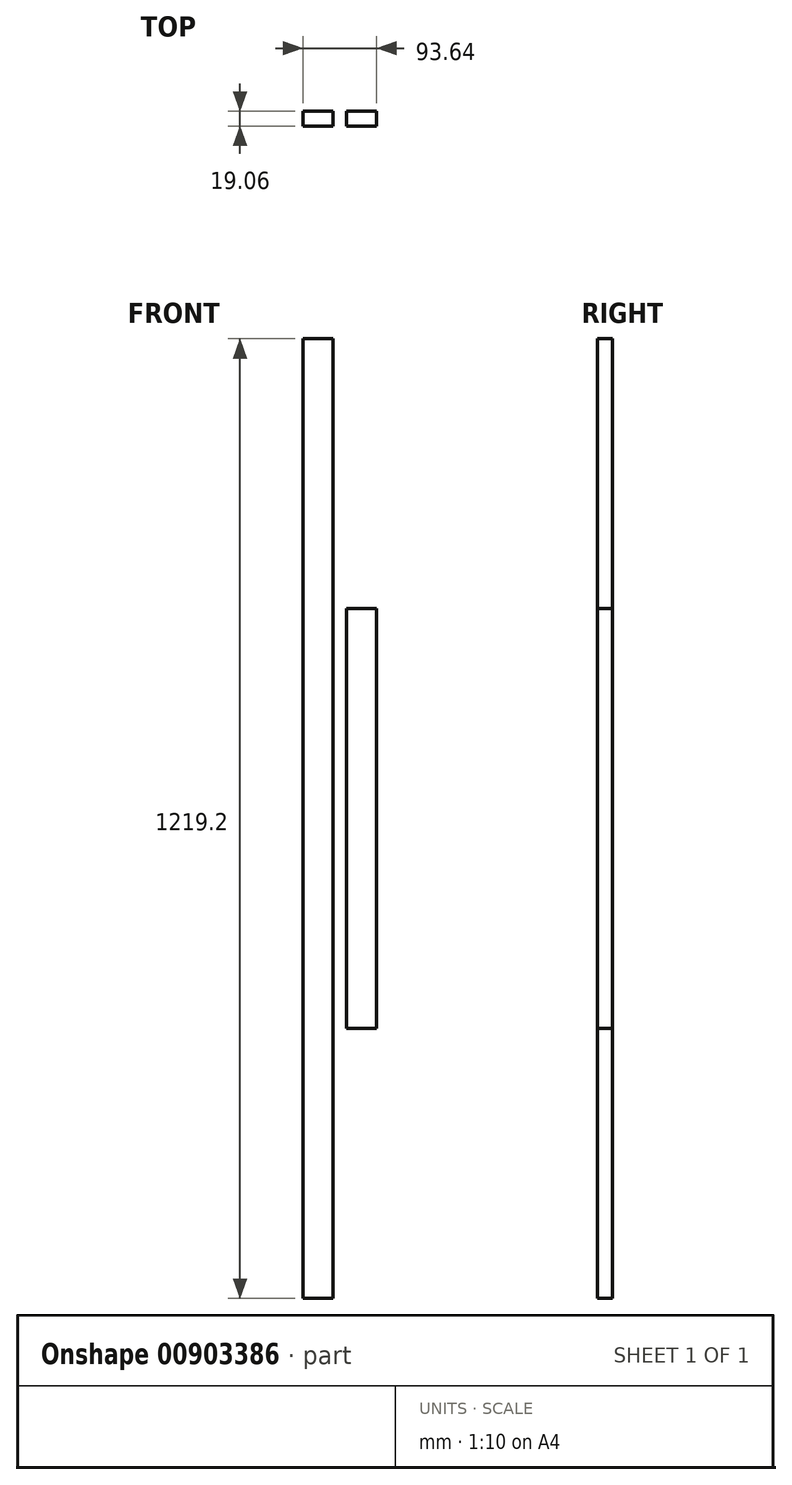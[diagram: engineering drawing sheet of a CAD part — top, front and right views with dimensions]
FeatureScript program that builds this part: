
annotation { "Feature Type Name" : "Feature", "Feature Type Description" : "" }
export const myFeature = defineFeature(function(context is Context, id is Id, definition is map)
    precondition{}
    {
        {
            var Q0;
            Q0=qCreatedBy(makeId("Top.planeOp"),FACE);
            var sketch = newSketch(context, id + "F0", { "sketchPlane" : qUnion([Q0])});
            skLineSegment(sketch, "E0.bottom", {"start": v(19.05, -9.53) * mm, "end": v(-19.05, -9.53) * mm});
            skLineSegment(sketch, "E0.top", {"start": v(19.05, 9.53) * mm, "end": v(-19.05, 9.53) * mm});
            skLineSegment(sketch, "E0.left", {"start": v(19.05, -9.53) * mm, "end": v(19.05, 9.52) * mm});
            skLineSegment(sketch, "E0.right", {"start": v(-19.05, -9.53) * mm, "end": v(-19.05, 9.52) * mm});
            skPoint(sketch, "E0.middle", {"position": v(0, 0) * mm});
            skSolve(sketch);
        }
        {
            var Q0;
            Q0=makeQuery(id+"F0.imprint","IMPRINT",FACE,{"disambiguationData":[TD([[makeQuery(id+"F0.imprint","IMPRINT",EDGE,{"derivedFrom":sQuery(id+"F0.wireOp",EDGE,"E0.bottom")}),-1.0]])]});
            extrude(context, id + "F1", {"entities" : qUnion([Q0]), "endBound" : BoundingType.SYMMETRIC, "depth" : 1219.2 * mm, "offsetDistance" : 25.4 * mm});
        }
        {
            var Q0;
            Q0=qCreatedBy(makeId("Top.planeOp"),FACE);
            var sketch = newSketch(context, id + "F2", { "sketchPlane" : qUnion([Q0])});
            skLineSegment(sketch, "E1.bottom", {"start": v(74.59, -9.52) * mm, "end": v(36.49, -9.52) * mm});
            skLineSegment(sketch, "E1.top", {"start": v(74.59, 9.53) * mm, "end": v(36.49, 9.53) * mm});
            skLineSegment(sketch, "E1.left", {"start": v(74.59, -9.52) * mm, "end": v(74.59, 9.53) * mm});
            skLineSegment(sketch, "E1.right", {"start": v(36.49, -9.52) * mm, "end": v(36.49, 9.53) * mm});
            skPoint(sketch, "E1.middle", {"position": v(55.54, 0) * mm});
            skSolve(sketch);
        }
        {
            var Q0;
            Q0 = qSketchRegion(id + "F2", true);
            extrude(context, id + "F3", {"entities" : qUnion([Q0]), "endBound" : BoundingType.SYMMETRIC, "depth" : 533.4 * mm, "offsetDistance" : 25.4 * mm});
        }
    });
